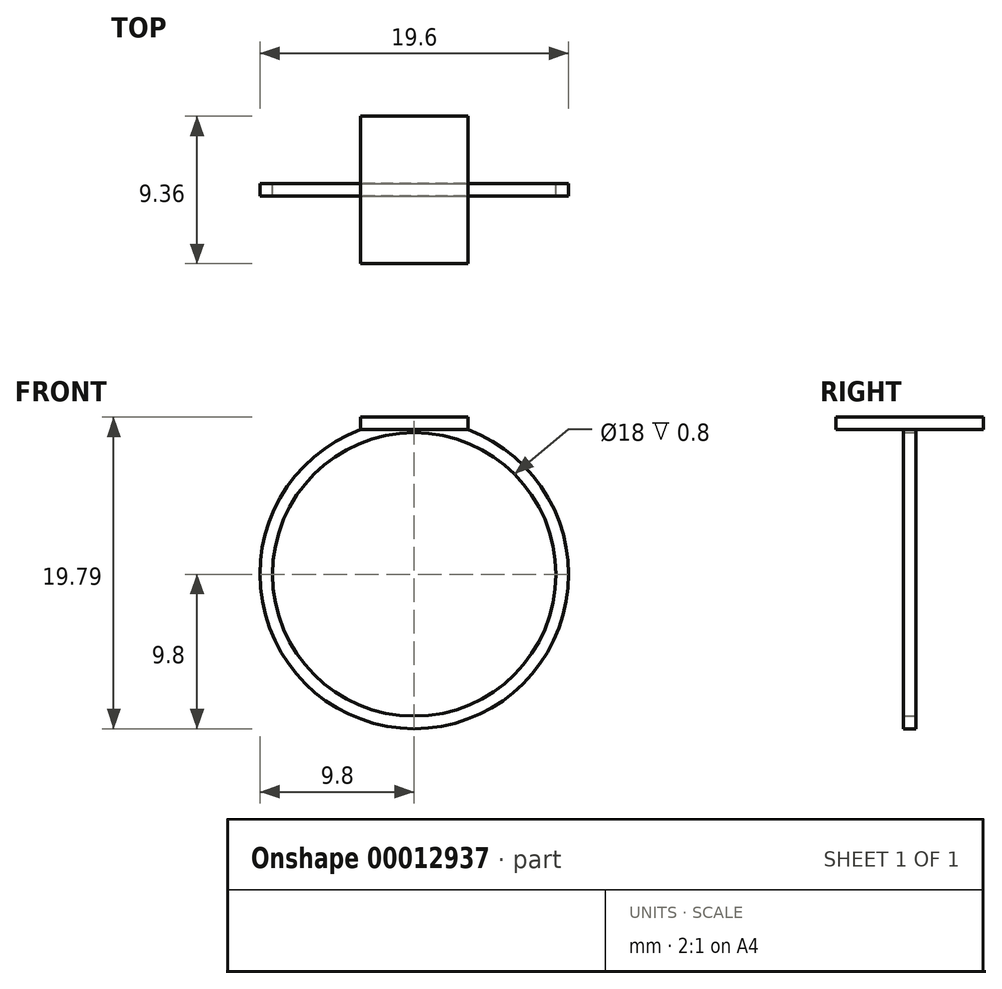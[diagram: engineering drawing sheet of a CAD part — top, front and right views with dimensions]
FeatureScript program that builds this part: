
annotation { "Feature Type Name" : "Feature", "Feature Type Description" : "" }
export const myFeature = defineFeature(function(context is Context, id is Id, definition is map)
    precondition{}
    {
        {
            var Q0;
            Q0=qCreatedBy(makeId("Front.planeOp"),FACE);
            var sketch = newSketch(context, id + "F0", { "sketchPlane" : qUnion([Q0])});
            skCircle(sketch, "E0", {"center": v(0, 0) * mm, "radius": 9 * mm});
            skCircle(sketch, "E1", {"center": v(0, 0) * mm, "radius": 9.8 * mm});
            skLineSegment(sketch, "E2", {"start": v(-3.4, 9.19) * mm, "end": v(3.4, 9.19) * mm});
            skLineSegment(sketch, "E3", {"start": v(0, 0) * mm, "end": v(3.4, 9.19) * mm});
            skLineSegment(sketch, "E4", {"start": v(-3.4, 9.19) * mm, "end": v(0, 0) * mm});
            skSolve(sketch);
        }
        {
            var Q0;
            {var subQ1=sQuery(id+"F0.wireOp",EDGE,"E0");var subQ6=sQuery(id+"F0.wireOp",EDGE,"E3");var subQ7=makeQuery(id+"F0.imprint","INTERSECT",VERTEX,{"derivedFrom":[subQ1,subQ6]});Q0=makeQuery(id+"F0.imprint","IMPRINT",FACE,{"disambiguationData":[TD([[makeQuery(id+"F0.imprint","IMPRINT",EDGE,{"disambiguationData":[TD([[subQ7,1.0]])],"derivedFrom":subQ1}),-1.0]])]});}
            var Q1;
            {var subQ4=sQuery(id+"F0.wireOp",EDGE,"E2");Q1=makeQuery(id+"F0.imprint","IMPRINT",FACE,{"disambiguationData":[TD([[makeQuery(id+"F0.imprint","IMPRINT",EDGE,{"derivedFrom":subQ4}),-1.0]])]});}
            extrude(context, id + "F1", {"entities" : qUnion([Q0, Q1]), "depth" : .4 * mm, "hasSecondDirection" : true, "secondDirectionOppositeDirection" : true, "secondDirectionDepth" : .4 * mm});
        }
        {
            var Q0;
            Q0=makeQuery(id+"F1.opExtrude","SWEPT_FACE",FACE,{"disambiguationData":[OSD([sQuery(id+"F0.wireOp",EDGE,"E2")])]});
            var sketch = newSketch(context, id + "F2", { "sketchPlane" : qUnion([Q0])});
            skLineSegment(sketch, "E5.rect.bottom", {"start": v(3.4, -4.68) * mm, "end": v(-3.4, -4.68) * mm});
            skLineSegment(sketch, "E5.rect.top", {"start": v(3.4, 4.68) * mm, "end": v(-3.4, 4.68) * mm});
            skLineSegment(sketch, "E5.rect.left", {"start": v(3.4, -4.68) * mm, "end": v(3.4, 4.68) * mm});
            skLineSegment(sketch, "E5.rect.right", {"start": v(-3.4, -4.68) * mm, "end": v(-3.4, 4.68) * mm});
            skPoint(sketch, "E5.rect.middle", {"position": v(0, 0) * mm});
            skSolve(sketch);
        }
        {
            var Q0;
            Q0=qSketchRegion(id+"F2",true);
            extrude(context, id + "F3", {"entities" : qUnion([Q0]), "operationType" : NewBodyOperationType.ADD, "depth" : .8 * mm});
        }
    });
